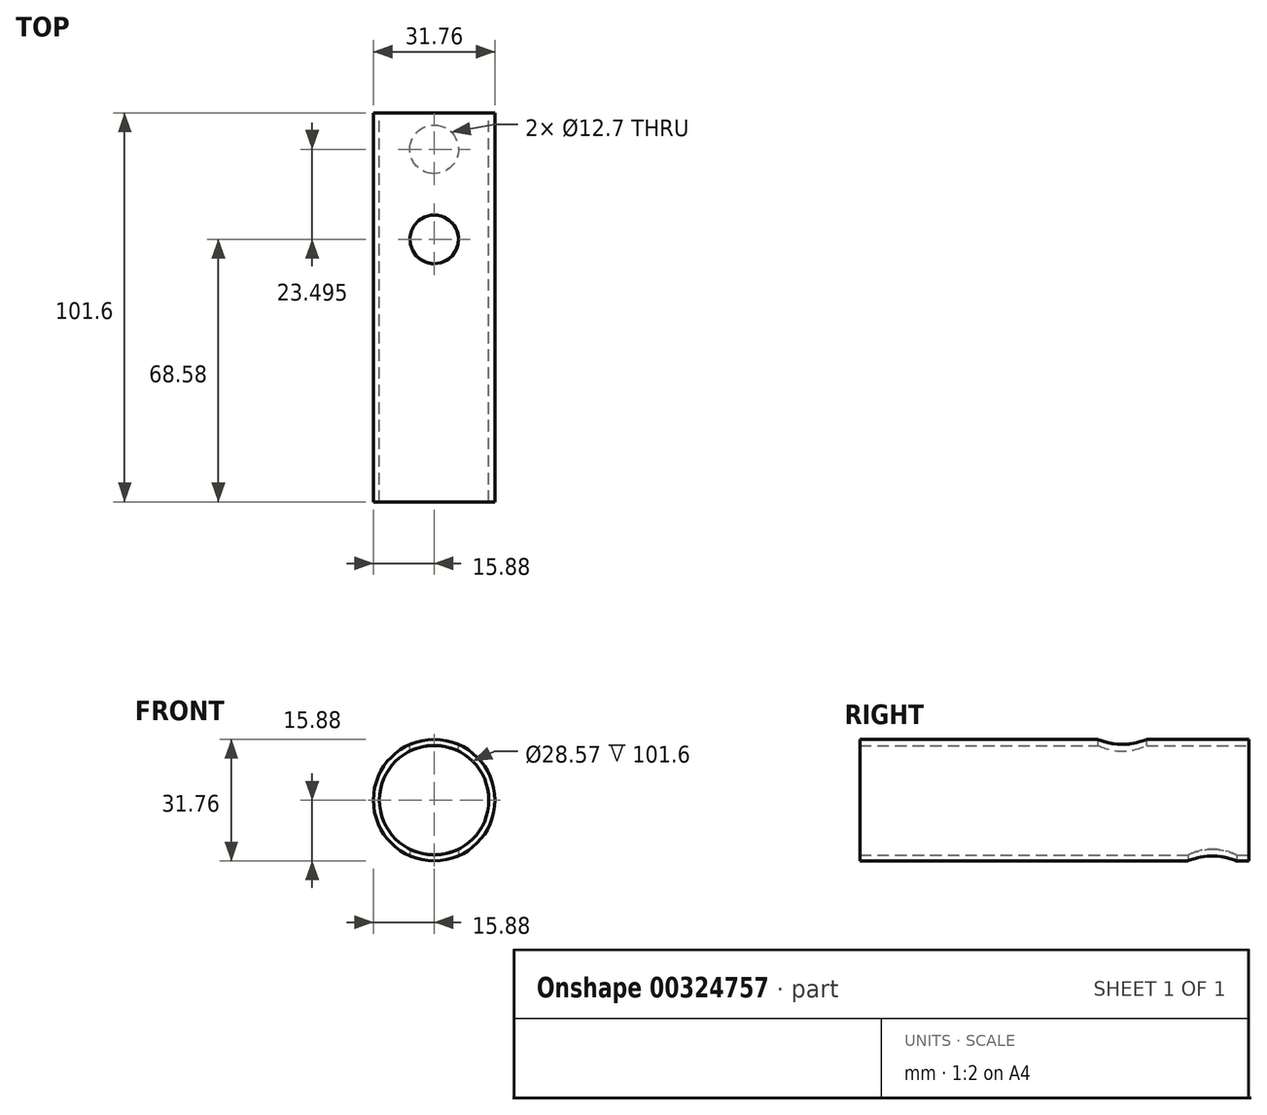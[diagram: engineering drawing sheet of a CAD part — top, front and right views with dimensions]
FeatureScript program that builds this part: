
annotation { "Feature Type Name" : "Feature", "Feature Type Description" : "" }
export const myFeature = defineFeature(function(context is Context, id is Id, definition is map)
    precondition{}
    {
        {
            var Q0;
            Q0=qCreatedBy(makeId("Front.planeOp"),FACE);
            var sketch = newSketch(context, id + "F0", { "sketchPlane" : qUnion([Q0])});
            skCircle(sketch, "E0", {"center": v(0, 0) * mm, "radius": 15.88 * mm});
            skCircle(sketch, "E1", {"center": v(0, 0) * mm, "radius": 14.29 * mm});
            skSolve(sketch);
        }
        {
            var Q0;
            Q0=makeQuery(id+"F0.imprint","IMPRINT",FACE,{"disambiguationData":[TD([[makeQuery(id+"F0.imprint","IMPRINT",EDGE,{"derivedFrom":sQuery(id+"F0.wireOp",EDGE,"E0")}),1.0]])]});
            extrude(context, id + "F1", {"entities" : qUnion([Q0]), "depth" : 101.6 * mm, "offsetDistance" : 25.4 * mm});
        }
        {
            var Q0;
            Q0=qCreatedBy(makeId("Top.planeOp"),FACE);
            cPlane(context, id + "F2", {"entities" : qUnion([Q0]), "cplaneType" : CPlaneType.OFFSET, "offset" : 28.57 * mm, "width" : 152.4 * mm, "height" : 152.4 * mm});
        }
        {
            var Q0;
            Q0=qCreatedBy(id+"F2.planeOp",FACE);
            var sketch = newSketch(context, id + "F3", { "sketchPlane" : qUnion([Q0])});
            skCircle(sketch, "E2", {"center": v(0, -33.02) * mm, "radius": 6.35 * mm});
            skSolve(sketch);
        }
        {
            var Q0;
            Q0=makeQuery(id+"F3.imprint","IMPRINT",FACE,{"disambiguationData":[TD([[makeQuery(id+"F3.imprint","IMPRINT",EDGE,{"derivedFrom":sQuery(id+"F3.wireOp",EDGE,"E2")}),1.0]])]});
            extrude(context, id + "F4", {"entities" : qUnion([Q0]), "operationType" : NewBodyOperationType.REMOVE, "oppositeDirection" : true, "depth" : 25.4 * mm, "offsetDistance" : 25.4 * mm});
        }
        {
            var Q0;
            Q0=qCreatedBy(makeId("Top.planeOp"),FACE);
            cPlane(context, id + "F5", {"entities" : qUnion([Q0]), "cplaneType" : CPlaneType.OFFSET, "offset" : 28.57 * mm, "oppositeDirection" : true, "width" : 152.4 * mm, "height" : 152.4 * mm});
        }
        {
            var Q0;
            Q0=qCreatedBy(id+"F5.planeOp",FACE);
            var sketch = newSketch(context, id + "F6", { "sketchPlane" : qUnion([Q0])});
            skCircle(sketch, "E3", {"center": v(0, -9.53) * mm, "radius": 6.35 * mm});
            skSolve(sketch);
        }
        {
            var Q0;
            Q0=makeQuery(id+"F6.imprint","IMPRINT",FACE,{"disambiguationData":[TD([[makeQuery(id+"F6.imprint","IMPRINT",EDGE,{"derivedFrom":sQuery(id+"F6.wireOp",EDGE,"E3")}),1.0]])]});
            extrude(context, id + "F7", {"entities" : qUnion([Q0]), "operationType" : NewBodyOperationType.REMOVE, "depth" : 25.4 * mm, "offsetDistance" : 25.4 * mm});
        }
    });
